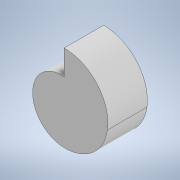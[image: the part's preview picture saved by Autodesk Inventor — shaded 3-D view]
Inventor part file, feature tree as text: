
AUTODESK INVENTOR PART (.ipt)
format: ipt  version: 2021 (Build 250183000, 183)  size: 104,960 bytes
history: native  units: in
note: dims shown in document units (in); Inventor stores cm internally (conversion verified against a paired STEP export)
features: extrude x1, sketch x1
ambient origin geometry x8: Origin, YZ Plane, XZ Plane, XY Plane, X Axis, Y Axis, Z Axis, Center Point
bodies: Solid1 (feature_tree)
feature tree (2):
  extrude  "Extrusion1"  Depth=0.1575in
  sketch  "Sketch2"  dims[d6=0.1969in d7=0.0984in d9=0.0246in d10=0.0492in d11=0.0738in d12=0.1575in d13=0.0in]
